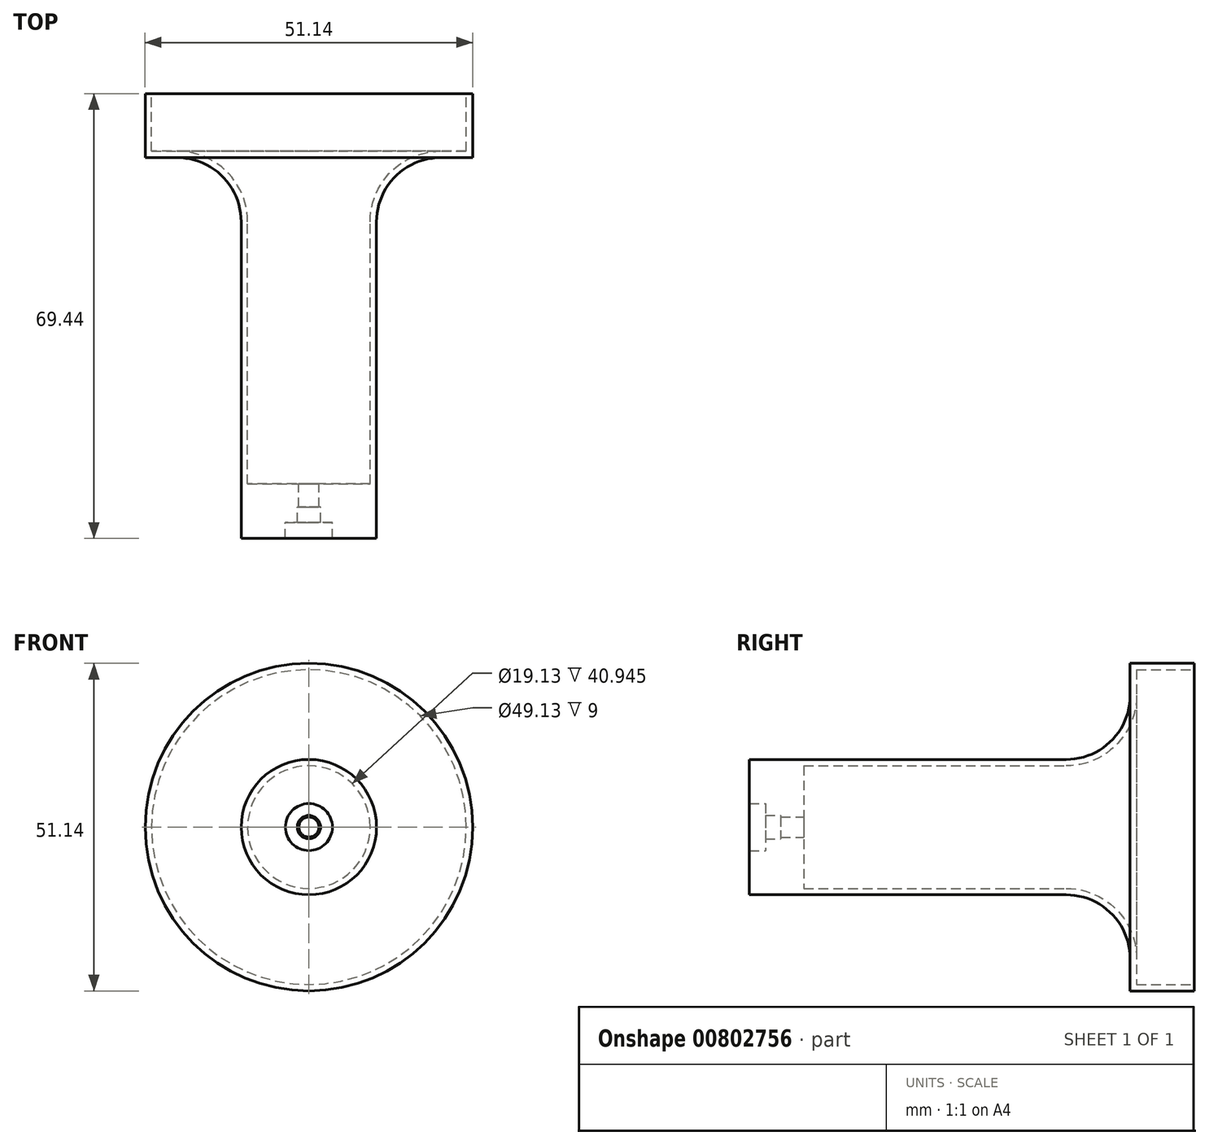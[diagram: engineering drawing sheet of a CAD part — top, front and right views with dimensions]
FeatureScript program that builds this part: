
annotation { "Feature Type Name" : "Feature", "Feature Type Description" : "" }
export const myFeature = defineFeature(function(context is Context, id is Id, definition is map)
    precondition{}
    {
        {
            var Q0;
            Q0=qCreatedBy(makeId("Top.planeOp"),FACE);
            var sketch = newSketch(context, id + "F0", { "sketchPlane" : qUnion([Q0])});
            skLineSegment(sketch, "E0", {"start": v(-24.57, 0) * mm, "end": v(-25.57, 0) * mm});
            skLineSegment(sketch, "E1", {"start": v(-25.57, 0) * mm, "end": v(-25.57, -10) * mm});
            skLineSegment(sketch, "E2", {"start": v(-25.57, -10) * mm, "end": v(-20.57, -10) * mm});
            skLineSegment(sketch, "E3", {"start": v(-3.67, -69.44) * mm, "end": v(-10.57, -69.44) * mm});
            skLineSegment(sketch, "E4", {"start": v(-10.57, -69.44) * mm, "end": v(-10.57, -20) * mm});
            skPoint(sketch, "E5.newPointB", {"position": v(0, -10) * mm});
            skArc(sketch, "E5.filletArc", {"start": v(-10.57, -20) * mm, "mid": v(-13.5, -12.93) * mm, "end": v(-20.57, -10) * mm});
            skLineSegment(sketch, "E6", {"start": v(-3.67, -69.44) * mm, "end": v(-3.67, -66.95) * mm});
            skLineSegment(sketch, "E7", {"start": v(-3.67, -66.95) * mm, "end": v(-1.82, -66.95) * mm});
            skLineSegment(sketch, "E8", {"start": v(-1.82, -66.95) * mm, "end": v(-1.82, -64.55) * mm});
            skLineSegment(sketch, "E9", {"start": v(-1.82, -64.55) * mm, "end": v(-1.57, -64.55) * mm});
            skLineSegment(sketch, "E10", {"start": v(-1.57, -64.55) * mm, "end": v(-1.57, -60.94) * mm});
            skLineSegment(sketch, "E11", {"start": v(0, 0) * mm, "end": v(0, -6.68) * mm});
            skLineSegment(sketch, "E12", {"start": v(-1.57, -60.94) * mm, "end": v(-9.57, -60.94) * mm});
            skLineSegment(sketch, "E13.0", {"start": v(-24.57, 0) * mm, "end": v(-24.57, -9) * mm});
            skLineSegment(sketch, "E13.1", {"start": v(-24.57, -9) * mm, "end": v(-20.57, -9) * mm});
            skArc(sketch, "E13.2", {"start": v(-9.57, -20) * mm, "mid": v(-12.79, -12.22) * mm, "end": v(-20.57, -9) * mm});
            skLineSegment(sketch, "E13.3", {"start": v(-9.57, -60.94) * mm, "end": v(-9.57, -20) * mm});
            skSolve(sketch);
        }
        {
            var Q0;
            Q0 = qSketchRegion(id + "F0", true);
            var Q1;
            Q1=sQuery(id+"F0.wireOp",EDGE,"E11");
            revolve(context, id + "F1", {"surfaceOperationType" : NewSurfaceOperationType.NEW, "entities" : qUnion([Q0]), "axis" : qUnion([Q1]), "revolveType" : RevolveType.FULL});
        }
    });
